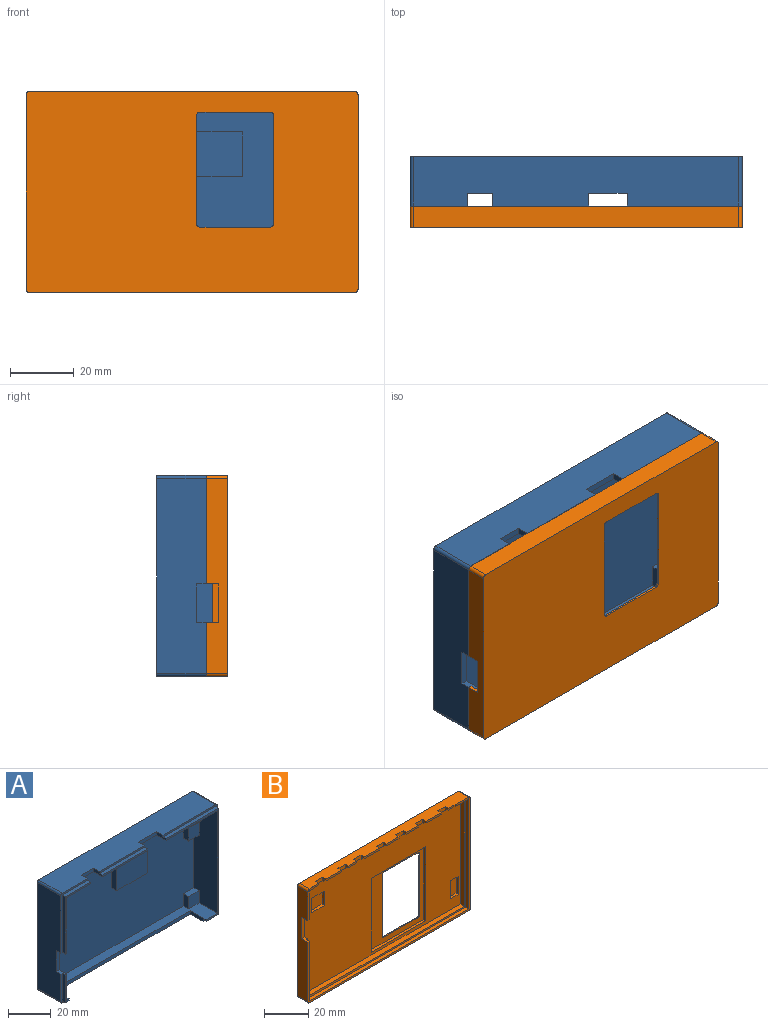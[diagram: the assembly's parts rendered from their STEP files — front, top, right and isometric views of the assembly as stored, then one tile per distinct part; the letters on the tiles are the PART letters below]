
ASSEMBLY  parts=2 mates=1
PART A: 61 faces, bbox 104x17.5x63 mm
  f0: plane 100x59mm, normal (0,-1,0), area 5323.8mm2, adj f1,f11,f13,f19,f27,f28,f29,f30
  f1: plane 100x15.5mm, normal (0,0,-1), area 1360mm2, adj f0,f2,f3,f8,f11,f13,f35,f50
  f2: plane 30x1mm, normal (0,-1,0), area 30mm2, adj f1,f6,f51,f53
  f3: plane 61x35mm, normal (0,-1,0), area 102.4mm2, adj f1,f7,f13,f19,f20,f41,f42,f50
  f4: plane 30x1mm, normal (0,-1,0), area 30mm2, adj f6,f15,f51,f53
  f5: plane 63x36mm, normal (0,-1,0), area 106mm2, adj f7,f15,f16,f17,f20,f25,f26,f41
  f6: plane 30x2mm, normal (0,0,1), area 60mm2, adj f2,f4,f51,f53
  f7: plane 35x2mm, normal (0,0,1), area 70mm2, adj f3,f5,f42,f50
  f8: plane 33x17mm, normal (0,-1,0), area 49mm2, adj f1,f11,f12,f43,f47,f54
  f9: plane 34x18mm, normal (0,-1,0), area 50.8mm2, adj f10,f12,f15,f23,f43,f47,f54
  f10: plane 61x15.5mm, normal (-1,0,0), area 909.5mm2, adj f9,f14,f18,f23,f24,f47,f48,f49
  f11: plane 59x15.5mm, normal (1,0,0), area 782.4mm2, adj f0,f1,f8,f19,f39,f40,f46,f47
  f12: plane 33x2mm, normal (-1,0,0), area 66mm2, adj f8,f9,f43,f47
  f13: plane 59x15.5mm, normal (-1,0,0), area 803.5mm2, adj f0,f1,f3,f19,f33,f34,f36,f37
  f14: plane 17x3.6mm, normal (0,-1,0), area 19.4mm2, adj f10,f16,f21,f24,f44,f45,f48
  f15: plane 102x15.5mm, normal (0,0,1), area 1501mm2, adj f4,f5,f9,f18,f23,f26,f50,f51
  f16: plane 102x15.5mm, normal (0,0,-1), area 807.5mm2, adj f5,f14,f18,f20,f21,f22,f24,f25
  f17: plane 61x15.5mm, normal (1,0,0), area 945.5mm2, adj f5,f18,f25,f26
  f18: plane 104x63mm, normal (0,1,0), area 6551.1mm2, adj f10,f15,f16,f17,f23,f24,f25,f26
  f19: plane 100x15.5mm, normal (0,0,1), area 552.9mm2, adj f0,f3,f11,f13,f20,f21,f22,f32
  f20: plane 10.5x2mm, normal (-1,0,0), area 19mm2, adj f3,f5,f16,f19,f22,f41
  f21: plane 10.5x2mm, normal (1,0,0), area 19mm2, adj f14,f16,f19,f22,f45,f46
  f22: plane 91x2mm, normal (0,-1,0), area 182mm2, adj f16,f19,f20,f21
  f23: cylinder r=1mm len=15.5mm, axis (0,-1,0), area 24.3mm2, adj f9,f10,f15,f18
  f24: cylinder r=1mm len=15.5mm, axis (0,1,0), area 24.3mm2, adj f10,f14,f16,f18
  f25: cylinder r=1mm len=15.5mm, axis (0,-1,0), area 24.3mm2, adj f5,f16,f17,f18
  f26: cylinder r=1mm len=15.5mm, axis (0,1,0), area 24.3mm2, adj f5,f15,f17,f18
  f27: plane 13.94x3.5mm, normal (-1,0,0), area 48.8mm2, adj f0,f28,f30,f31
  f28: plane 20.52x3.5mm, normal (0,0,-1), area 71.8mm2, adj f0,f27,f29,f31
  f29: plane 13.94x3.5mm, normal (1,0,0), area 48.8mm2, adj f0,f28,f30,f31
  f30: plane 20.52x3.5mm, normal (0,0,1), area 71.8mm2, adj f0,f27,f29,f31
  f31: plane 20.52x13.94mm, normal (0,-1,0), area 286.1mm2, adj f27,f28,f29,f30
  f32: plane 7x3.5mm, normal (-1,0,0), area 24.5mm2, adj f0,f19,f33,f34
  f33: plane 7x3.5mm, normal (0,0,1), area 24.5mm2, adj f0,f13,f32,f34
  f34: plane 7x7mm, normal (0,-1,0), area 49mm2, adj f13,f19,f32,f33
  f35: plane 20x5mm, normal (-1,0,0), area 86.5mm2, adj f0,f1,f36,f37,f56,f57
  f36: plane 7x3.5mm, normal (0,0,-1), area 24.5mm2, adj f0,f13,f35,f37
  f37: plane 9x7mm, normal (0,-1,0), area 63mm2, adj f13,f35,f36,f56
  f38: plane 4.9x3.5mm, normal (1,0,0), area 17.1mm2, adj f0,f19,f39,f40
  f39: plane 4.9x3.5mm, normal (0,0,1), area 17.1mm2, adj f0,f11,f38,f40
  f40: plane 4.9x4.9mm, normal (0,-1,0), area 24mm2, adj f11,f19,f38,f39
  f41: plane 8.4x2mm, normal (0,0,-1), area 16.8mm2, adj f3,f5,f20,f42
  f42: plane 61x2mm, normal (1,0,0), area 122mm2, adj f3,f5,f7,f41
  f43: plane 17x2mm, normal (0,0,1), area 34mm2, adj f8,f9,f12,f54
  f44: plane 16x2mm, normal (-1,0,0), area 32mm2, adj f14,f45,f46,f48
  f45: plane 2.6x2mm, normal (0,0,-1), area 5.2mm2, adj f14,f21,f44,f46
  f46: plane 16x2.6mm, normal (0,-1,0), area 17.6mm2, adj f11,f19,f21,f44,f45,f48
  f47: plane 5x2mm, normal (0,0,-1), area 8mm2, adj f8,f9,f10,f11,f12,f49
  f48: plane 5x2mm, normal (0,0,1), area 8mm2, adj f10,f11,f14,f44,f46,f49
  f49: plane 12x2mm, normal (0,-1,0), area 24mm2, adj f10,f11,f47,f48
  f50: plane 6x2mm, normal (-1,0,0), area 10mm2, adj f1,f3,f5,f7,f15,f52
  f51: plane 6x2mm, normal (1,0,0), area 10mm2, adj f1,f2,f4,f6,f15,f52
  f52: plane 12x2mm, normal (0,-1,0), area 24mm2, adj f1,f15,f50,f51
  f53: plane 6x2mm, normal (-1,0,0), area 10mm2, adj f1,f2,f4,f6,f15,f55
  f54: plane 6x2mm, normal (1,0,0), area 10mm2, adj f1,f8,f9,f15,f43,f55
  f55: plane 8x2mm, normal (0,-1,0), area 16mm2, adj f1,f15,f53,f54
  f56: plane 7x1.5mm, normal (0,0,-1), area 10.5mm2, adj f13,f35,f37,f57
  f57: plane 11x7mm, normal (0,-1,0), area 77mm2, adj f1,f13,f35,f56
  f58: plane 11x5mm, normal (1,0,0), area 55mm2, adj f0,f1,f59,f60
  f59: plane 7x5mm, normal (0,0,-1), area 35mm2, adj f0,f11,f58,f60
  f60: plane 11x7mm, normal (0,-1,0), area 77mm2, adj f1,f11,f58,f59
PART B: 93 faces, bbox 104x6.6x63 mm
  f0: plane 3.8x1mm, normal (0,-1,0), area 3.8mm2, adj f7,f14,f43,f90
  f1: plane 9.62x1mm, normal (0,-1,0), area 9.6mm2, adj f14,f28,f87,f91
  f2: plane 5.56x1mm, normal (0,-1,0), area 5.6mm2, adj f8,f14,f84,f88
  f3: plane 9.62x1mm, normal (0,-1,0), area 9.6mm2, adj f9,f14,f81,f85
  f4: plane 8.1x1mm, normal (0,-1,0), area 8.1mm2, adj f10,f14,f78,f82
  f5: plane 8.1x1mm, normal (0,-1,0), area 8.1mm2, adj f11,f14,f75,f79
  f6: plane 9.62x1mm, normal (0,-1,0), area 9.6mm2, adj f12,f14,f72,f76
  f7: plane 6.4x2mm, normal (0,0,-1), area 11.3mm2, adj f0,f15,f29,f36,f43,f90
  f8: plane 5.56x1.6mm, normal (0,0,-1), area 8.9mm2, adj f2,f16,f84,f88
  f9: plane 9.62x1.6mm, normal (0,0,-1), area 15.4mm2, adj f3,f17,f81,f85
  f10: plane 8.1x1.6mm, normal (0,0,-1), area 13mm2, adj f4,f18,f78,f82
  f11: plane 8.1x1.6mm, normal (0,0,-1), area 13mm2, adj f5,f19,f75,f79
  f12: plane 9.62x1.6mm, normal (0,0,-1), area 15.4mm2, adj f6,f20,f72,f76
  f13: plane 12.77x2mm, normal (0,0,-1), area 23.8mm2, adj f21,f25,f34,f44,f45,f73
  f14: plane 102x6.6mm, normal (0,0,1), area 572.4mm2, adj f0,f1,f2,f3,f4,f5,f6,f23
  f15: plane 16x6.4mm, normal (0,-1,0), area 21.4mm2, adj f7,f22,f31,f36,f46,f90
  f16: plane 5.56x1mm, normal (0,-1,0), area 5.6mm2, adj f8,f22,f84,f88
  f17: plane 9.62x1mm, normal (0,-1,0), area 9.6mm2, adj f9,f22,f81,f85
  f18: plane 8.1x1mm, normal (0,-1,0), area 8.1mm2, adj f10,f22,f78,f82
  f19: plane 8.1x1mm, normal (0,-1,0), area 8.1mm2, adj f11,f22,f75,f79
  f20: plane 9.62x1mm, normal (0,-1,0), area 9.6mm2, adj f12,f22,f72,f76
  f21: plane 102x61mm, normal (0,-1,0), area 205.8mm2, adj f13,f22,f26,f31,f32,f33,f34,f35
  f22: plane 100x2.6mm, normal (0,0,-1), area 247.1mm2, adj f15,f16,f17,f18,f19,f20,f21,f24
  f23: plane 104x63mm, normal (0,1,0), area 5688mm2, adj f14,f27,f37,f38,f39,f40,f41,f42
  f24: plane 100x59mm, normal (0,-1,0), area 4351mm2, adj f22,f31,f32,f33,f49,f50,f51,f52
  f25: plane 104x63mm, normal (0,-1,0), area 206.8mm2, adj f13,f14,f26,f27,f34,f35,f37,f38
  f26: plane 33x2mm, normal (1,0,0), area 66mm2, adj f21,f25,f35,f48
  f27: plane 61x6.6mm, normal (-1,0,0), area 354.6mm2, adj f23,f25,f29,f41,f42,f46,f47,f48
  f28: plane 9.62x1.6mm, normal (0,0,-1), area 15.4mm2, adj f1,f30,f87,f91
  f29: plane 17x3.6mm, normal (0,-1,0), area 19.4mm2, adj f7,f14,f27,f36,f42,f43,f46
  f30: plane 9.62x1mm, normal (0,-1,0), area 9.6mm2, adj f22,f28,f87,f91
  f31: plane 59x2.6mm, normal (1,0,0), area 129.4mm2, adj f15,f21,f22,f24,f32,f46,f47,f48
  f32: plane 100x2.6mm, normal (0,0,1), area 260mm2, adj f21,f24,f31,f33
  f33: plane 59x2.6mm, normal (-1,0,0), area 153.4mm2, adj f21,f22,f24,f32
  f34: plane 61x2mm, normal (-1,0,0), area 122mm2, adj f13,f21,f25,f35
  f35: plane 102x2mm, normal (0,0,1), area 204mm2, adj f21,f25,f26,f34
  f36: plane 16x2mm, normal (1,0,0), area 32mm2, adj f7,f15,f29,f46
  f37: cylinder r=1mm len=6.6mm, axis (0,1,0), area 10.4mm2, adj f14,f23,f25,f38
  f38: plane 61x6.6mm, normal (1,0,0), area 402.6mm2, adj f23,f25,f37,f39
  f39: cylinder r=1mm len=6.6mm, axis (0,-1,0), area 10.4mm2, adj f23,f25,f38,f40
  f40: plane 102x6.6mm, normal (0,0,-1), area 673.2mm2, adj f23,f25,f39,f41
  f41: cylinder r=1mm len=6.6mm, axis (0,1,0), area 10.4mm2, adj f23,f25,f27,f40
  f42: cylinder r=1mm len=6.6mm, axis (0,-1,0), area 10.4mm2, adj f14,f23,f27,f29
  f43: plane 1x0.4mm, normal (1,0,0), area 0.4mm2, adj f0,f7,f14,f29
  f44: plane 1x0.4mm, normal (-1,0,0), area 0.4mm2, adj f13,f14,f25,f45
  f45: plane 4.37x1mm, normal (0,-1,0), area 4.4mm2, adj f13,f14,f44,f73
  f46: plane 4x2mm, normal (0,0,-1), area 6mm2, adj f15,f27,f29,f31,f36,f47
  f47: plane 12x2mm, normal (0,-1,0), area 24mm2, adj f27,f31,f46,f48
  f48: plane 4x2mm, normal (0,0,1), area 6mm2, adj f21,f25,f26,f27,f31,f47
  f49: plane 35x1.4mm, normal (0,0,-1), area 49mm2, adj f24,f50,f52,f53
  f50: plane 41x1.4mm, normal (1,0,0), area 57.4mm2, adj f24,f49,f51,f53
  f51: plane 35x1.4mm, normal (0,0,1), area 49mm2, adj f24,f50,f52,f53
  f52: plane 41x1.4mm, normal (-1,0,0), area 57.4mm2, adj f24,f49,f51,f53
  f53: plane 41x35mm, normal (0,-1,0), area 571.9mm2, adj f49,f50,f51,f52,f64,f65,f66,f67
  f54: plane 5x1.4mm, normal (0,0,-1), area 7mm2, adj f24,f55,f57,f58
  f55: plane 10x1.4mm, normal (1,0,0), area 14mm2, adj f24,f54,f56,f58
  f56: plane 5x1.4mm, normal (0,0,1), area 7mm2, adj f24,f55,f57,f58
  f57: plane 10x1.4mm, normal (-1,0,0), area 14mm2, adj f24,f54,f56,f58
  f58: plane 10x5mm, normal (0,-1,0), area 50mm2, adj f54,f55,f56,f57
  f59: plane 8x1.4mm, normal (0,0,-1), area 11.2mm2, adj f24,f60,f62,f63
  f60: plane 8x1.4mm, normal (1,0,0), area 11.2mm2, adj f24,f59,f61,f63
  f61: plane 8x1.4mm, normal (0,0,1), area 11.2mm2, adj f24,f60,f62,f63
  f62: plane 8x1.4mm, normal (-1,0,0), area 11.2mm2, adj f24,f59,f61,f63
  f63: plane 8x8mm, normal (0,-1,0), area 64mm2, adj f59,f60,f61,f62
  f64: plane 22x0.6mm, normal (0,0,-1), area 13.2mm2, adj f23,f53,f68,f71
  f65: plane 34x0.6mm, normal (1,0,0), area 20.4mm2, adj f23,f53,f68,f69
  f66: plane 22x0.6mm, normal (0,0,1), area 13.2mm2, adj f23,f53,f69,f70
  f67: plane 34x0.6mm, normal (-1,0,0), area 20.4mm2, adj f23,f53,f70,f71
  f68: cylinder r=1mm len=1mm, axis (0,-1,0), area 0.9mm2, adj f23,f53,f64,f65
  f69: cylinder r=1mm len=1mm, axis (0,1,0), area 0.9mm2, adj f23,f53,f65,f66
  f70: cylinder r=1mm len=1mm, axis (0,-1,0), area 0.9mm2, adj f23,f53,f66,f67
  f71: cylinder r=1mm len=1mm, axis (0,1,0), area 0.9mm2, adj f23,f53,f64,f67
  f72: plane 2x2mm, normal (1,0,0), area 2.4mm2, adj f6,f12,f14,f20,f22,f74
  f73: plane 2x2mm, normal (-1,0,0), area 2.4mm2, adj f13,f14,f21,f22,f45,f74
  f74: plane 4.6x2mm, normal (0,-1,0), area 9.2mm2, adj f14,f22,f72,f73
  f75: plane 2x2mm, normal (1,0,0), area 2.4mm2, adj f5,f11,f14,f19,f22,f77
  f76: plane 2x2mm, normal (-1,0,0), area 2.4mm2, adj f6,f12,f14,f20,f22,f77
  f77: plane 4.6x2mm, normal (0,-1,0), area 9.2mm2, adj f14,f22,f75,f76
  f78: plane 2x2mm, normal (1,0,0), area 2.4mm2, adj f4,f10,f14,f18,f22,f80
  f79: plane 2x2mm, normal (-1,0,0), area 2.4mm2, adj f5,f11,f14,f19,f22,f80
  f80: plane 4.6x2mm, normal (0,-1,0), area 9.2mm2, adj f14,f22,f78,f79
  f81: plane 2x2mm, normal (1,0,0), area 2.4mm2, adj f3,f9,f14,f17,f22,f83
  f82: plane 2x2mm, normal (-1,0,0), area 2.4mm2, adj f4,f10,f14,f18,f22,f83
  f83: plane 4.6x2mm, normal (0,-1,0), area 9.2mm2, adj f14,f22,f81,f82
  f84: plane 2x2mm, normal (1,0,0), area 2.4mm2, adj f2,f8,f14,f16,f22,f86
  f85: plane 2x2mm, normal (-1,0,0), area 2.4mm2, adj f3,f9,f14,f17,f22,f86
  f86: plane 4.6x2mm, normal (0,-1,0), area 9.2mm2, adj f14,f22,f84,f85
  f87: plane 2x2mm, normal (1,0,0), area 2.4mm2, adj f1,f14,f22,f28,f30,f89
  f88: plane 2x2mm, normal (-1,0,0), area 2.4mm2, adj f2,f8,f14,f16,f22,f89
  f89: plane 4.6x2mm, normal (0,-1,0), area 9.2mm2, adj f14,f22,f87,f88
  f90: plane 2x2mm, normal (1,0,0), area 2.4mm2, adj f0,f7,f14,f15,f22,f92
  f91: plane 2x2mm, normal (-1,0,0), area 2.4mm2, adj f1,f14,f22,f28,f30,f92
  f92: plane 4.6x2mm, normal (0,-1,0), area 9.2mm2, adj f14,f22,f90,f91
PLACE A t=(-35.37,-45.71,16.96)mm
PLACE B rot(axis=(1,0,0),180deg) t=(-35.37,-63.81,38.47)mm
MATE fastened A.f1 <-> B.f32  axis (0,0,1) through (1.48,-61.21,57.21)mm
